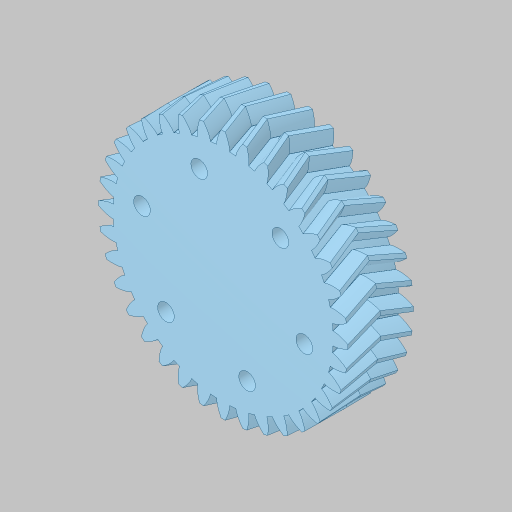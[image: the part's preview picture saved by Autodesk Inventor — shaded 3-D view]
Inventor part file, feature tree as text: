
AUTODESK INVENTOR PART (.ipt)
format: ipt  version: 2023.5 (Build 275446000, 446)  size: 1,216,512 bytes
history: native  units: in
note: dims shown in document units (in); Inventor stores cm internally (conversion verified against a paired STEP export)
features: hole x1, sketch x1, other x1, projected_geometry x1
ambient origin geometry x8: Origin, YZ Plane, XZ Plane, XY Plane, X Axis, Y Axis, Z Axis, Center Point
bodies: Solid1 (feature_tree)
feature tree (4):
  hole  "Hole1"  [1 undecoded]
  sketch  "Sketch1"  dims[d0=2.8148in d1=2.0in d2=2.3622in d4=360.0deg d6=0.201in d7=0.75in d8=0.385in d9=0.25in d10=0.5635in d11=1.0in d12=0.8108in]
  other  "Helical 2M 36T"
  projected_geometry  "Project Cut Edges1"
note: 1 required parameter value undecoded (feature->parameter linkage not recoverable at this tier; creation-order binding heuristic only, values carry confidence <= 0.55)
